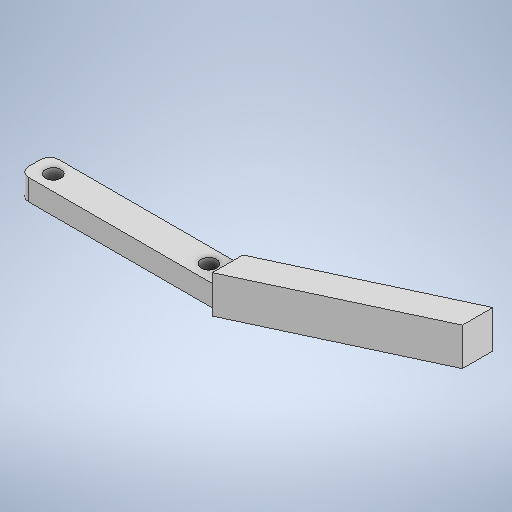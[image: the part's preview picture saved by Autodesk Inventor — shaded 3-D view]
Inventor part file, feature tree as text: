
AUTODESK INVENTOR PART (.ipt)
format: ipt  version: 2025.1 (Build 291241020, 241B)  size: 757,248 bytes
history: native  units: in
note: dims shown in document units (in); Inventor stores cm internally (conversion verified against a paired STEP export)
features: extrude x17, sketch x17, other x3, fillet x3, pattern_circular x1
ambient origin geometry x8: Origin, YZ Plane, XZ Plane, XY Plane, X Axis, Y Axis, Z Axis, Center Point
bodies: Solid1 (feature_tree)
feature tree (41):
  other  "servoMoldAssembly.iam"
  other  "block.ipt:1"
  other  "sg90horn.ipt:1"
  extrude  "Extrusion1"  Depth=0.3937in TaperAngle=0.0deg
  extrude  "Extrusion2"  Depth=0.3937in TaperAngle=0.0deg
  extrude  "Extrusion3"  Depth=0.0591in TaperAngle=0.0deg
  extrude  "Extrusion4"  Depth=0.0591in TaperAngle=0.0deg
  extrude  "Extrusion5"  Depth=1.9685in
  extrude  "Extrusion6"  Depth=0.3937in TaperAngle=0.0deg
  extrude  "Extrusion7"  Depth=0.2362in TaperAngle=0.0deg
  extrude  "Extrusion8"  Depth=0.2362in
  extrude  "Extrusion10"  Depth=0.2362in TaperAngle=0.0deg
  extrude  "Extrusion11"  Depth=0.2362in TaperAngle=0.0deg
  fillet  "Fillet1"  Radius=0.0787in
  extrude  "Extrusion12"  Depth=0.8268in
  fillet  "Fillet2"  Radius=1.1934in
  extrude  "Extrusion13"  TaperAngle=90.0deg  [1 undecoded]
  pattern_circular  "Circular Pattern2"  Count=20 Angle=240.0deg
  extrude  "Extrusion14"  Depth=0.3937in
  extrude  "Extrusion15"  Depth=0.3937in
  extrude  "Extrusion16"  Depth=0.0787in
  fillet  "Fillet3"  Radius=1.3032in
  extrude  "Extrusion17"  Depth=0.2362in
  extrude  "Extrusion19"  Depth=0.2362in
  sketch  "Sketch3"  dims[d0=0.3937in d1=0.3937in d2=0.0in]
  sketch  "Sketch4"  dims[d3=0.2795in d4=0.3937in d5=0.0in]
  sketch  "Sketch5"  dims[d6=0.0591in d7=0.0in d8=0.0591in d9=0.0in]
  sketch  "Sketch6"  dims[d10=0.0591in d11=0.0in d12=0.0591in d13=0.0in]
  sketch  "Sketch7"  dims[d14=1.4173in d15=1.9685in]
  sketch  "Sketch8"  dims[d16=0.0in d17=0.3937in d18=0.0in]
  sketch  "Sketch9"  dims[d19=0.3937in d20=0.0in d29=0.2362in d30=0.0in]
  sketch  "Sketch10"  dims[d31=0.2362in d32=0.1299in]
  sketch  "Sketch12"  dims[d33=0.0787in d34=0.2362in d35=0.0in]
  sketch  "Sketch13"  dims[d36=0.0787in d37=0.2362in d38=0.0in d39=0.0787in]
  sketch  "Sketch14"  dims[d40=0.0984in d41=0.8268in d42=1.1934in]
  sketch  "Sketch15"  dims[d43=0.0591in d44=90.0deg]
  sketch  "Sketch16"  dims[d45=0.3937in d46=0.0in d47=7.874in d48=240.0deg]
  sketch  "Sketch17"  dims[d50=0.3937in d51=0.0in d52=0.1299in]
  sketch  "Sketch18"  dims[d53=0.3937in d54=0.0in d55=0.1575in]
  sketch  "Sketch19"  dims[d56=0.3937in d57=0.0in d58=0.0787in d60=1.3032in]
  sketch  "Sketch20"  dims[d61=0.1299in d62=0.1575in d63=0.0in d64=0.3937in d65=0.0in d70=0.0984in d75=1.5748in d76=0.1718in d77=1.5748in d78=0.1718in d79=0.0787in d80=0.2362in d81=0.0in d82=0.0in]
note: 1 required parameter value undecoded (feature->parameter linkage not recoverable at this tier; creation-order binding heuristic only, values carry confidence <= 0.55)
